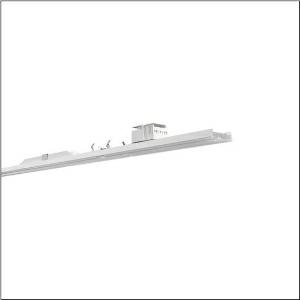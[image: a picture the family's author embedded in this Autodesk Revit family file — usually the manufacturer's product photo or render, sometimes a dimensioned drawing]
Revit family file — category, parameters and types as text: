
# Revit family: licross_r__11_recessed_extreme_ho_51tl18dn4c5le_a815
name_source: partatom
category: Lighting Fixtures
units: mm (PartAtom-declared; Revit-internal decimal feet)

## family parameters
Cut with Voids When Loaded = No
Host = Face
Light Source = No
Part Type = Normal
Room Calculation Point = No
Round Connector Dimension = Use Diameter
Shared = No

## types (1)
- --- (1 x LED, 12830 lm, 76 W, 4000K)
    Apparent Load = 76 VA
    CIE Flux Codes = 78 94 99 100 100
    Color Rendering = 80
    Color Temperature = 4000K
    Default Elevation = 1800 mm
    Description = Licross® 11 Recessed extreme HOluminaire insert, length: 1.500mm, width: 66mm, height: 67mm, LED rated luminous flux: 12.830lm, light colour: 840, control gear: DALI 2, control gear: ECG DALI, with plug, 5-pole, with phase selection, mains connection: 220..240V, AC, 50/60Hz, halogen-free wiring, primary optical cover: cover, of PMMA, light emission: direct distribution, protection rating (complete): IP40, insulation class (complete): insulation class I (protective earthing), certification: CE, ENEC, VDE, protection symbol: D if used in an environment without relevant dust loads with corresponding accessories, permissible ambient temperature for indoor applications: -25..+45°C, reducing of maximum allowable ambient temperature of 5°C with ceiling mounting, corresponds to IFS (International Featured Standards) requirements for safety and quality in the food industry, packaging unit: 1 piece
    Height = 58 mm
    Lamp = 1 x LED
    Lamp Light Flux = 12830 lm
    Lamp Power = 76 W
    Lamp count = 1
    Length = 1500 mm
    Luminous efficacy = 169 lm/W
    Manufacturer = Siteco
    ModVariant = No
    Model = 51TL18DN4C5LE
    Mounting Place = Ceiling
    Mounting Type = Pendant
    Number of Poles = 1
    OnlyDefault = Yes
    Power Factor = 1
    Product Name = Licross® 11 Recessed extreme HO
    Product group = luminaire insert
    ProductGroupID = 902
    Protection Class = Protection class I
    Protection Degree = IP 40
    RLX_Detail_Level = 1
    RlxData = <blob elided: 22233 chars, md5=5238548e>
    Socket = socket
    Standby Power = 0 W
    System Light Flux = 12830 lm
    System Power = 76 W
    Type Comments = factory setting: luminous flux: 100 % | dim-lin: 254 | 430 mA
    Type Image = l_1266722.jpg
    URL = http://relux.com
    VarID = @adj_132554
    Voltage = 0 V
    Weight = 0.00 kg
    Width = 66 mm

## geometry (parser evidence)
native form markers: Blend x4, Sweep x9
no freeform markers — native parametric forms only
